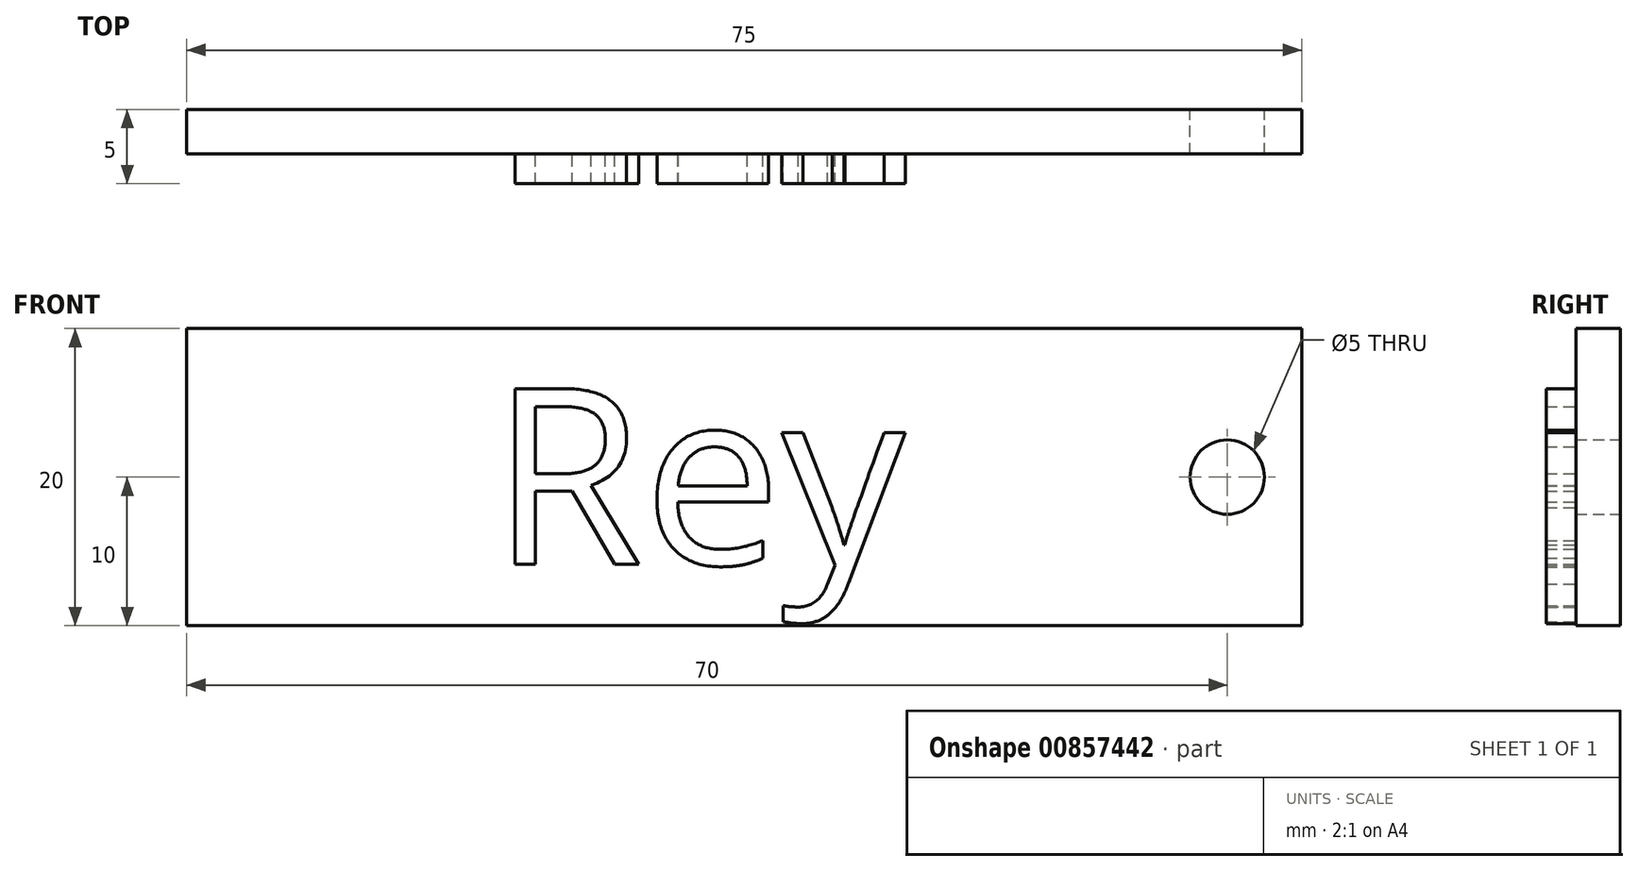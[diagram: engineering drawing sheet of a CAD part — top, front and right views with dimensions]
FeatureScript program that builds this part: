
annotation { "Feature Type Name" : "Feature", "Feature Type Description" : "" }
export const myFeature = defineFeature(function(context is Context, id is Id, definition is map)
    precondition{}
    {
        {
            var Q0;
            Q0=qCreatedBy(makeId("Front.planeOp"),FACE);
            var sketch = newSketch(context, id + "F0", { "sketchPlane" : qUnion([Q0])});
            skLineSegment(sketch, "E0.bottom", {"start": v(0, -2.9) * mm, "end": v(0, -2.9) * mm});
            skLineSegment(sketch, "E0.top", {"start": v(0, 0) * mm, "end": v(0, 0) * mm});
            skLineSegment(sketch, "E0.left", {"start": v(0, -2.9) * mm, "end": v(0, 0) * mm});
            skLineSegment(sketch, "E0.right", {"start": v(0, -2.9) * mm, "end": v(0, 0) * mm});
            skLineSegment(sketch, "E1.bottom", {"start": v(0, 0) * mm, "end": v(75, 0) * mm});
            skLineSegment(sketch, "E1.top", {"start": v(0, -20) * mm, "end": v(75, -20) * mm});
            skLineSegment(sketch, "E1.left", {"start": v(0, 0) * mm, "end": v(0, -20) * mm});
            skLineSegment(sketch, "E1.right", {"start": v(75, 0) * mm, "end": v(75, -20) * mm});
            skCircle(sketch, "E2", {"center": v(70, -10) * mm, "radius": 2.5 * mm});
            skSolve(sketch);
        }
        {
            var Q0;
            {var subQ1=sQuery(id+"F0.wireOp",EDGE,"E1.bottom");Q0=makeQuery(id+"F0.imprint","IMPRINT",FACE,{"disambiguationData":[TD([[makeQuery(id+"F0.imprint","IMPRINT",EDGE,{"derivedFrom":subQ1}),-1.0]])]});}
            extrude(context, id + "F1", {"entities" : qUnion([Q0]), "depth" : 3 * mm, "offsetDistance" : 25 * mm});
        }
        {
            var Q0;
            Q0=makeQuery(id+"F1.opExtrude","CAP_FACE",FACE,{"disambiguationData":[OSD([sQuery(id+"F0.wireOp",EDGE,"E1.bottom"),sQuery(id+"F0.wireOp",EDGE,"E1.top"),sQuery(id+"F0.wireOp",EDGE,"E1.left"),sQuery(id+"F0.wireOp",EDGE,"E1.right"),sQuery(id+"F0.wireOp",EDGE,"E2")])],"isStart":false});
            var sketch = newSketch(context, id + "F2", { "sketchPlane" : qUnion([Q0])});
            skText(sketch, "E3", { "text": "Rey", "fontName": "OpenSans-Regular.ttf"});
            const initialGuessF2  = {"E3": [0.02045, -0.01588, 1, 0, 0.01194]};
            skSetInitialGuess(sketch, initialGuessF2);
            skSolve(sketch);
        }
        {
            var Q0;
            Q0 = qSketchRegion(id + "F2", true);
            extrude(context, id + "F3", {"entities" : qUnion([Q0]), "operationType" : NewBodyOperationType.ADD, "depth" : 2 * mm, "offsetDistance" : 25 * mm});
        }
    });
